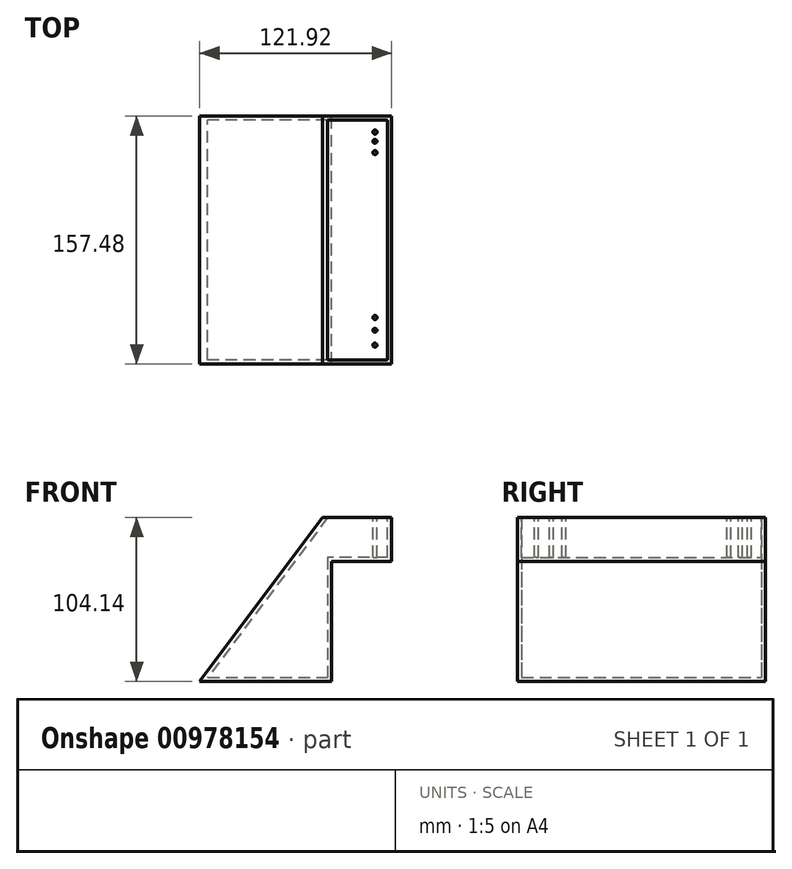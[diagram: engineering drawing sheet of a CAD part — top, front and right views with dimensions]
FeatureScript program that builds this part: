
annotation { "Feature Type Name" : "Feature", "Feature Type Description" : "" }
export const myFeature = defineFeature(function(context is Context, id is Id, definition is map)
    precondition{}
    {
        {
            var Q0;
            Q0=qCreatedBy(makeId("Front.planeOp"),FACE);
            var sketch = newSketch(context, id + "F0", { "sketchPlane" : qUnion([Q0])});
            skLineSegment(sketch, "E0", {"start": v(0, 50.8) * mm, "end": v(-56.8, 0) * mm});
            skLineSegment(sketch, "E1", {"start": v(-56.8, 0) * mm, "end": v(19.4, 0) * mm});
            skLineSegment(sketch, "E2", {"start": v(0, 50.8) * mm, "end": v(19.4, 0) * mm});
            skSolve(sketch);
        }
        {
            var Q0;
            Q0=qCreatedBy(makeId("Front.planeOp"),FACE);
            var sketch = newSketch(context, id + "F1", { "sketchPlane" : qUnion([Q0])});
            skLineSegment(sketch, "E3", {"start": v(0, 101.6) * mm, "end": v(0, 0) * mm});
            skLineSegment(sketch, "E4", {"start": v(0, 101.6) * mm, "end": v(-76.2, 0) * mm});
            skLineSegment(sketch, "E5", {"start": v(-76.2, 0) * mm, "end": v(0, 0) * mm});
            skLineSegment(sketch, "E6", {"start": v(0, 101.6) * mm, "end": v(38.1, 101.6) * mm});
            skLineSegment(sketch, "E7", {"start": v(38.1, 76.2) * mm, "end": v(0, 76.2) * mm});
            skLineSegment(sketch, "E8", {"start": v(38.1, 76.2) * mm, "end": v(38.1, 101.6) * mm});
            skSolve(sketch);
        }
        {
            var Q0;
            {var subQ0=sQuery(id+"F1.wireOp",EDGE,"E4");Q0=makeQuery(id+"F1.imprint","IMPRINT",FACE,{"disambiguationData":[TD([[makeQuery(id+"F1.imprint","IMPRINT",EDGE,{"derivedFrom":subQ0}),1.0]])]});}
            var Q1;
            {var subQ0=sQuery(id+"F1.wireOp",EDGE,"E6");Q1=makeQuery(id+"F1.imprint","IMPRINT",FACE,{"disambiguationData":[TD([[makeQuery(id+"F1.imprint","IMPRINT",EDGE,{"derivedFrom":subQ0}),-1.0]])]});}
            extrude(context, id + "F2", {"entities" : qUnion([Q0, Q1]), "depth" : 152.4 * mm, "offsetDistance" : 25.4 * mm});
        }
        {
            var Q0;
            Q0=makeQuery(id+"F2.opExtrude","SWEPT_FACE",FACE,{"disambiguationData":[OSD([sQuery(id+"F1.wireOp",EDGE,"E6")])]});
            var sketch = newSketch(context, id + "F3", { "sketchPlane" : qUnion([Q0])});
            skPoint(sketch, "E9", {"position": v(30, -7.65) * mm});
            skPoint(sketch, "E10", {"position": v(30, -13.51) * mm});
            skPoint(sketch, "E11", {"position": v(30, -20.73) * mm});
            skPoint(sketch, "E12", {"position": v(30, -143) * mm});
            skPoint(sketch, "E13", {"position": v(30, -133.53) * mm});
            skPoint(sketch, "E14", {"position": v(30, -125.4) * mm});
            skSolve(sketch);
        }
        {
            var Q0;
            Q0=sQuery(id+"F3.wireOp",VERTEX,"E9");
            var Q1;
            Q1=sQuery(id+"F3.wireOp",VERTEX,"E10");
            var Q2;
            Q2=sQuery(id+"F3.wireOp",VERTEX,"E11");
            var Q3;
            Q3=sQuery(id+"F3.wireOp",VERTEX,"E13");
            var Q4;
            Q4=sQuery(id+"F3.wireOp",VERTEX,"E14");
            var Q5;
            Q5=sQuery(id+"F3.wireOp",VERTEX,"E12");
            var Q6;
            Q6=makeQuery(id+"F2.opExtrude","SWEPT_BODY",BODY,{"disambiguationData":[OSD([sQuery(id+"F1.wireOp",EDGE,"E3"),sQuery(id+"F1.wireOp",EDGE,"E4"),sQuery(id+"F1.wireOp",EDGE,"E5"),sQuery(id+"F1.wireOp",EDGE,"E6"),sQuery(id+"F1.wireOp",EDGE,"E7"),sQuery(id+"F1.wireOp",EDGE,"E8")])]});
            hole(context, id + "F4", {"style" : HoleStyle.SIMPLE, "endStyle" : HoleEndStyle.BLIND, "holeDiameter" : 2.54 * mm, "majorDiameter" : 6.35 * mm, "holeDepth" : 76.2 * mm, "isTappedThrough" : true, "tappedDepth" : 12.7 * mm, "tapClearance" : 3, "locations" : qUnion([Q0, Q1, Q2, Q3, Q4, Q5]), "scope" : qUnion([Q6])});
        }
        {
            var Q0;
            Q0=makeQuery(id+"F2.opExtrude","SWEPT_FACE",FACE,{"disambiguationData":[OSD([sQuery(id+"F1.wireOp",EDGE,"E6")])]});
            shell(context, id + "F5", {"entities" : qUnion([Q0]), "thickness" : 2.54 * mm, "oppositeDirection" : true});
        }
    });
